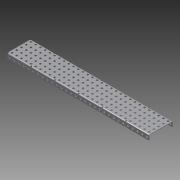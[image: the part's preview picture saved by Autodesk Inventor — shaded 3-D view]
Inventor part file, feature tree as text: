
AUTODESK INVENTOR PART (.ipt)
format: ipt  version: 2012 (Build 160160000, 160)  size: 2,473,472 bytes
history: native  units: in
note: dims shown in document units (in); Inventor stores cm internally (conversion verified against a paired STEP export)
features: other x1, imported_body x1, plane x1, split x1
ambient origin geometry x8: Origin, YZ Plane, XZ Plane, XY Plane, X Axis, Y Axis, Z Axis, Center Point
feature tree (4):
  parser-record x1  (decoder bookkeeping rows leaked as tree rows — omitted from the tree; the rows remain in map.json)
  imported_body  "Base1"
  plane  "Work Plane1"
  split  "Split1"
